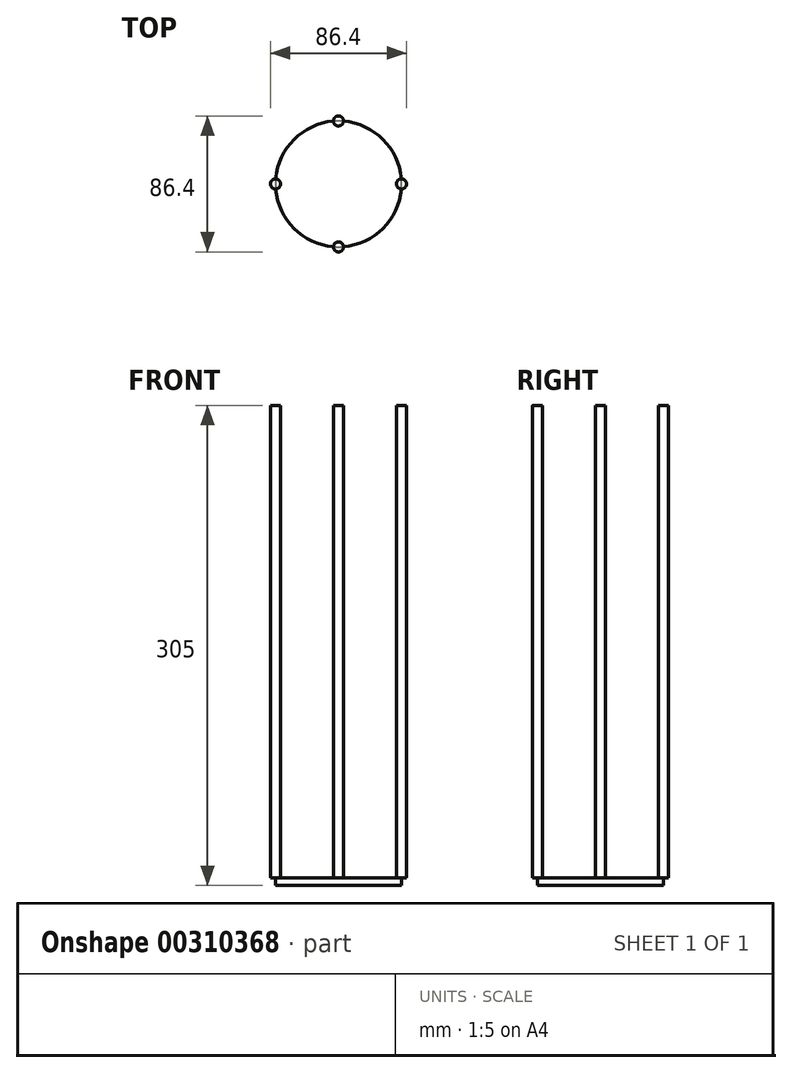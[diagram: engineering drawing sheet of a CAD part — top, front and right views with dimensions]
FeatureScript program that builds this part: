
annotation { "Feature Type Name" : "Feature", "Feature Type Description" : "" }
export const myFeature = defineFeature(function(context is Context, id is Id, definition is map)
    precondition{}
    {
        {
            var Q0;
            Q0=qCreatedBy(makeId("Top.planeOp"),FACE);
            var sketch = newSketch(context, id + "F0", { "sketchPlane" : qUnion([Q0])});
            skCircle(sketch, "E0", {"center": v(0, 0) * mm, "radius": 40 * mm});
            skSolve(sketch);
        }
        {
            var Q0;
            Q0 = qSketchRegion(id + "F0", true);
            extrude(context, id + "F1", {"entities" : qUnion([Q0]), "depth" : 5 * mm});
        }
        {
            var Q0;
            Q0=makeQuery(id+"F1.opExtrude","CAP_FACE",FACE,{"disambiguationData":[OSD([sQuery(id+"F0.wireOp",EDGE,"E0")])],"isStart":false});
            var sketch = newSketch(context, id + "F2", { "sketchPlane" : qUnion([Q0])});
            skCircle(sketch, "E1", {"center": v(0, 40) * mm, "radius": 3.2 * mm});
            skCircle(sketch, "E2", {"center": v(-40, 0) * mm, "radius": 3.2 * mm});
            skCircle(sketch, "E3", {"center": v(0, -40) * mm, "radius": 3.2 * mm});
            skCircle(sketch, "E4", {"center": v(40, 0) * mm, "radius": 3.2 * mm});
            skSolve(sketch);
        }
        {
            var Q0;
            Q0 = qSketchRegion(id + "F2", true);
            extrude(context, id + "F3", {"entities" : qUnion([Q0]), "operationType" : NewBodyOperationType.ADD, "depth" : 300 * mm});
        }
    });
